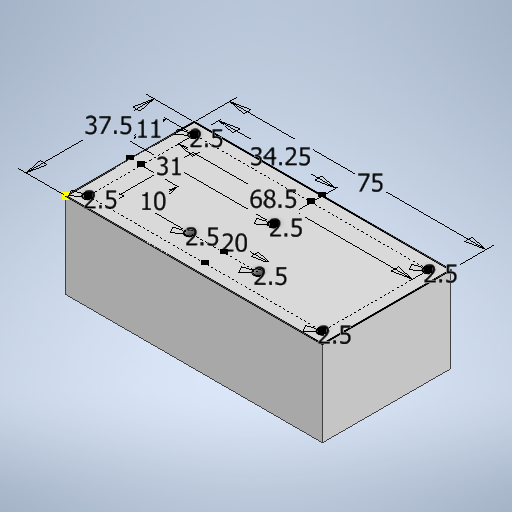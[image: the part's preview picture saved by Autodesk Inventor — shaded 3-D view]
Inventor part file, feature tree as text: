
AUTODESK INVENTOR PART (.ipt)
format: ipt  version: 2025.3 (Build 293356000, 356)  size: 537,600 bytes
history: native  units: in
note: dims shown in document units (in); Inventor stores cm internally (conversion verified against a paired STEP export)
features: extrude x2, sketch x1
ambient origin geometry x8: Origin, YZ Plane, XZ Plane, XY Plane, X Axis, Y Axis, Z Axis, Center Point
bodies: Solid1 (feature_tree)
feature tree (3):
  sketch  "Sketch1"  dims[d0=1.4764in d1=2.9528in d2=1.2205in d3=2.6969in d4=0.0984in d6=0.0984in d7=0.0984in d8=0.0984in d9=0.0984in d10=1.3484in d11=0.4331in d12=0.9843in d13=0.0in d14=0.315in d15=0.0in d16=0.0984in d17=0.0984in d18=0.7874in d19=0.3937in]
  extrude  "Extrusion1"  Depth=2.9528in
  extrude  "Extrusion2"  Depth=0.3937in
